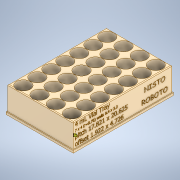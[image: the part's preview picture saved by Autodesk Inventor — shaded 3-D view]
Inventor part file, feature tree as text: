
AUTODESK INVENTOR PART (.ipt)
format: ipt  version: 2020 (Build 240168000, 168)  size: 2,329,088 bytes
history: native  units: in
note: dims shown in document units (in); Inventor stores cm internally (conversion verified against a paired STEP export)
features: sketch x3, extrude x2, hole x1, pattern_linear x1, fillet x1, emboss x1
ambient origin geometry x8: Origin, YZ Plane, XZ Plane, XY Plane, X Axis, Y Axis, Z Axis, Center Point
bodies: Solid1 (feature_tree)
feature tree (9):
  extrude  "Extrusion1"  TaperAngle=45.0deg  [1 undecoded]
  extrude  "Extrusion2"  TaperAngle=225.0deg  [1 undecoded]
  hole  "Hole2"  [1 undecoded]
  pattern_linear  "Rectangular Pattern1"  Spacing1=0.75in  [1 undecoded]
  fillet  "Fillet1"  [1 undecoded]
  emboss  "Emboss2"
  sketch  "Sketch1"  dims[d3=0.0in d5=45.0deg]
  sketch  "Sketch2"  dims[d6=0.0591in d7=225.0deg]
  sketch  "Sketch5"  dims[d9=0.0in d32=0.685in d33=0.75in d34=0.375in d35=0.25in d36=0.5635in d38=0.0in d41=0.7016in d44=0.812in d48=0.0394in d49=0.0in d50=0.4263in d51=0.3535in]
note: 5 required parameter values undecoded (feature->parameter linkage not recoverable at this tier; creation-order binding heuristic only, values carry confidence <= 0.55)
